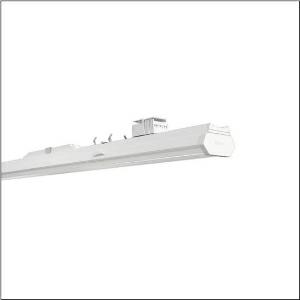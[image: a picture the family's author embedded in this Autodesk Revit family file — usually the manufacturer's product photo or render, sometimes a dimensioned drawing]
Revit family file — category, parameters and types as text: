
# Revit family: licross_11_protected_mo_51tp12dn695g
name_source: partatom
category: Lighting Fixtures
units: mm (PartAtom-declared; Revit-internal decimal feet)

## family parameters
Cut with Voids When Loaded = No
Host = Face
Light Source = No
Part Type = Normal
Room Calculation Point = No
Round Connector Dimension = Use Diameter
Shared = No

## types (1)
- --- (1 x LED, 9730 lm, 57.1 W, 6500K)
    Apparent Load = 57 VA
    CIE Flux Codes = 73 92 98 99 100
    Color Rendering = 80
    Color Temperature = 6500K
    Default Elevation = 1800 mm
    Description = Licross 11 Protected MO, luminaire insert, of sheet steel, galvanised, coil coated, white, length: 1.500mm, width: 90mm, height: 101mm, LED rated luminous flux: 9.730lm, light colour: 865, SDCM (Standard Deviation of Colour Matching)MacAdam ≤ 2 SDCM (initial), control gear: DALI 2, with plug, 5-pole, with phase selection, mains connection: 220..240V, AC, 50/60Hz, rated input power: 57W, internal wiring halogen-free, primary optical cover: cover, of PMMA, light emission: direct distribution, primary light characteristic: symmetric, protection rating (complete): IP64, insulation class (complete): insulation class I (protective earthing), certification: CE, ENEC, VDE, UKCA, protection symbol: D if used in an environment with conductive dust loads with corresponding accessories, impact resistance: IK06, permissible ambient temperature for indoor applications: -25..+35°C, corresponds to IFS (International Featured Standards) requirements for safety and quality in the food industry, reducing of maximum allowable ambient temperature of 5°C with ceiling mounting, LABS conformity tested according to VDMA 24364:2018-05, The light source and the operating device comply with the requirements of the Ecodesign Regulation (EU) 2019/2020 and are replaceable in accordance with this regulation, packaging unit: 1 piece
    Height = 92 mm
    Lamp = 1 x LED
    Lamp Light Flux = 9730 lm
    Lamp Power = 57.1 W
    Lamp count = 1
    Length = 1500 mm
    Luminous efficacy = 170 lm/W
    Manufacturer = Siteco
    ModVariant = No
    Model = 51TP12DN695G
    Mounting Place = Ceiling
    Mounting Type = Pendant
    Number of Poles = 1
    OnlyDefault = Yes
    Power Factor = 1
    Product Name = Licross 11 Protected MO
    Product group = luminaire insert | ceiling pendant
    ProductGroupID = 901
    Protection Class = Protection class I
    Protection Degree = IP 64
    RLX_Detail_Level = 1
    RLX_Emergency_Light_Flux = 0 lm
    RLX_Emergency_Type = 0
    RLX_Emergency_Type_DB = No
    RlxData = <blob elided: 24661 chars, md5=273d266b>
    Socket = socket
    Standby Power = 0 W
    System Light Flux = 9730 lm
    System Power = 57 W
    Type Comments = factory setting: luminous flux: 100 % | dim-lin: 254 | 378 mA
    Type Image = l_1256148.jpg
    URL = http://relux.com
    VarID = @adj_085303
    Voltage = 0 V
    Weight = 0.00 kg
    Width = 88 mm

## geometry (parser evidence)
native form markers: Blend x4, Sweep x8
no freeform markers — native parametric forms only
